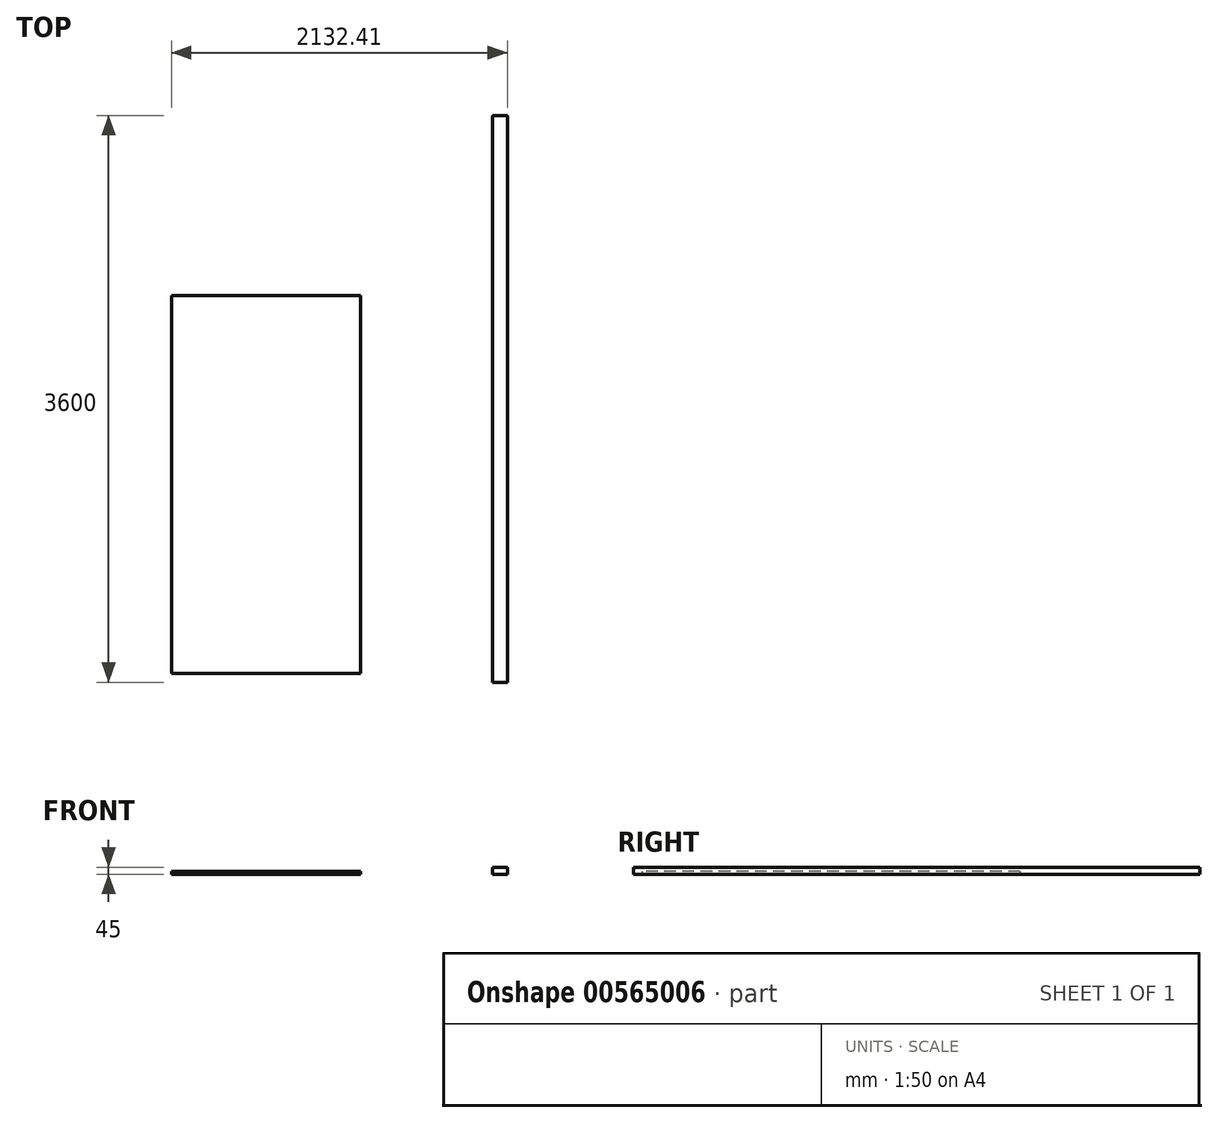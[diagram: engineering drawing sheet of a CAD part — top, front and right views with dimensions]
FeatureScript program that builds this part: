
annotation { "Feature Type Name" : "Feature", "Feature Type Description" : "" }
export const myFeature = defineFeature(function(context is Context, id is Id, definition is map)
    precondition{}
    {
        {
            var Q0;
            Q0=qCreatedBy(makeId("Top.planeOp"),FACE);
            var sketch = newSketch(context, id + "F0", { "sketchPlane" : qUnion([Q0])});
            skLineSegment(sketch, "E0.bottom", {"start": v(1643.2, 3381.4) * mm, "end": v(1738.2, 3381.4) * mm});
            skLineSegment(sketch, "E0.top", {"start": v(1643.2, -218.6) * mm, "end": v(1738.2, -218.6) * mm});
            skLineSegment(sketch, "E0.left", {"start": v(1643.2, 3381.4) * mm, "end": v(1643.2, -218.6) * mm});
            skLineSegment(sketch, "E0.right", {"start": v(1738.2, 3381.4) * mm, "end": v(1738.2, -218.6) * mm});
            skLineSegment(sketch, "E1.bottom", {"start": v(-394.2, 2238.23) * mm, "end": v(805.8, 2238.23) * mm});
            skLineSegment(sketch, "E1.top", {"start": v(-394.2, -161.77) * mm, "end": v(805.8, -161.77) * mm});
            skLineSegment(sketch, "E1.left", {"start": v(-394.2, 2238.23) * mm, "end": v(-394.2, -161.77) * mm});
            skLineSegment(sketch, "E1.right", {"start": v(805.8, 2238.23) * mm, "end": v(805.8, -161.77) * mm});
            skSolve(sketch);
        }
        {
            var Q0;
            Q0=makeQuery(id+"F0.imprint","IMPRINT",FACE,{"disambiguationData":[TD([[makeQuery(id+"F0.imprint","IMPRINT",EDGE,{"derivedFrom":sQuery(id+"F0.wireOp",EDGE,"E0.bottom")}),-1.0]])]});
            extrude(context, id + "F1", {"entities" : qUnion([Q0]), "depth" : 45 * mm, "offsetDistance" : 25 * mm});
        }
        {
            var Q0;
            Q0=makeQuery(id+"F0.imprint","IMPRINT",FACE,{"disambiguationData":[TD([[makeQuery(id+"F0.imprint","IMPRINT",EDGE,{"derivedFrom":sQuery(id+"F0.wireOp",EDGE,"E1.bottom")}),-1.0]])]});
            extrude(context, id + "F2", {"entities" : qUnion([Q0]), "depth" : 18 * mm, "offsetDistance" : 25 * mm});
        }
    });
